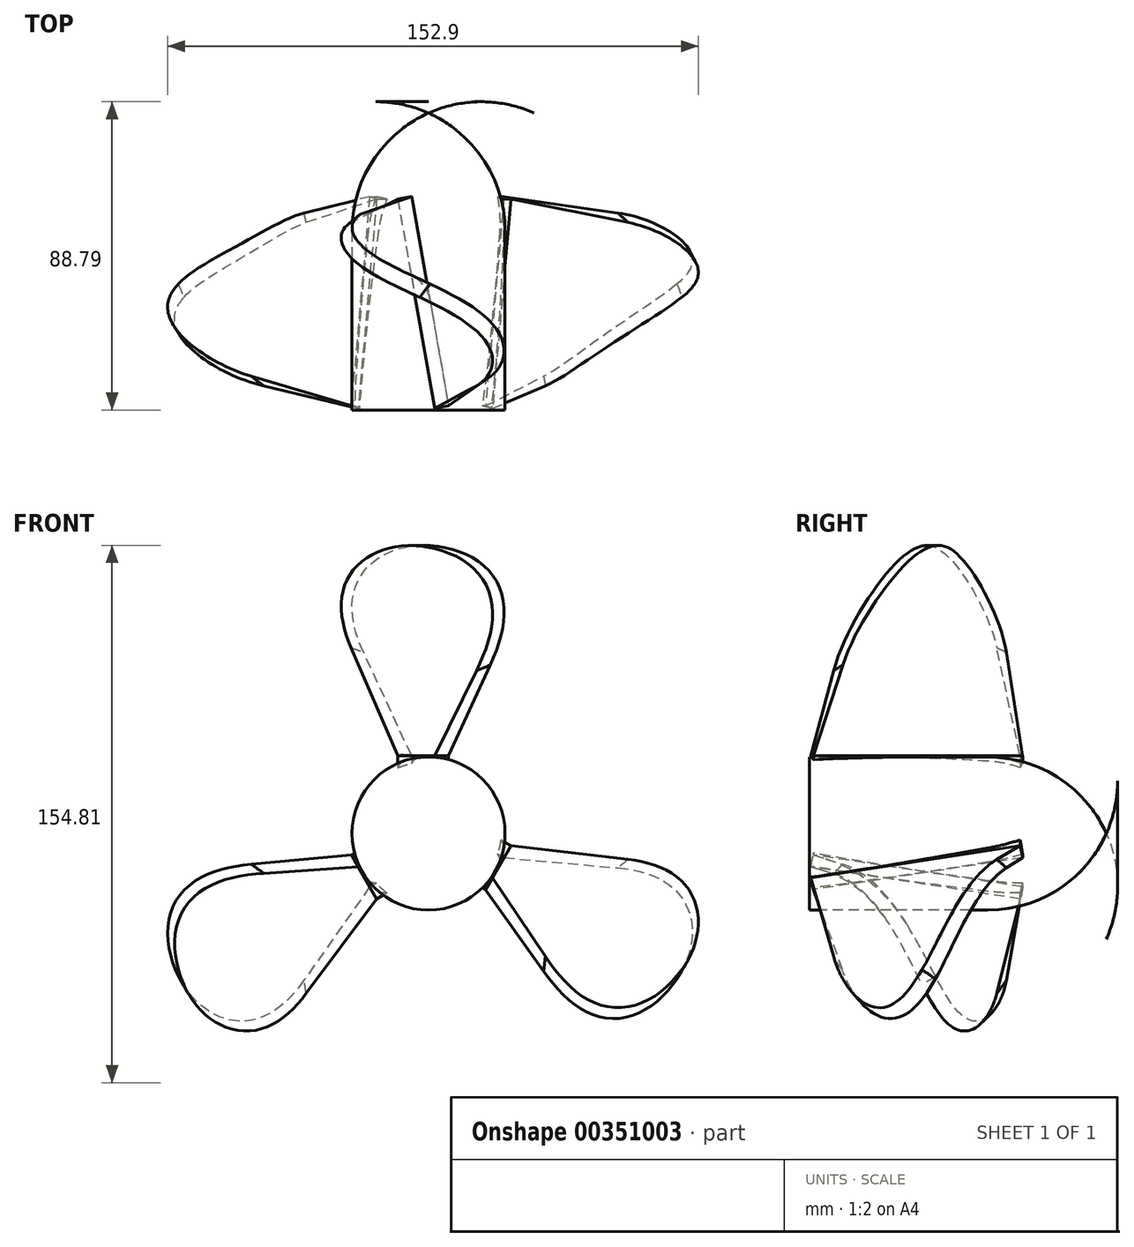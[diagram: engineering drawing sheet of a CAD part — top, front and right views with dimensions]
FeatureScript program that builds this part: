
annotation { "Feature Type Name" : "Feature", "Feature Type Description" : "" }
export const myFeature = defineFeature(function(context is Context, id is Id, definition is map)
    precondition{}
    {
        {
            var Q0;
            Q0=qCreatedBy(makeId("Right.planeOp"),FACE);
            var sketch = newSketch(context, id + "F0", { "sketchPlane" : qUnion([Q0])});
            skLineSegment(sketch, "E0", {"start": v(-50.75, 0) * mm, "end": v(-50.75, 22.06) * mm});
            skLineSegment(sketch, "E1", {"start": v(-50.75, 22.06) * mm, "end": v(0, 22.06) * mm});
            skLineSegment(sketch, "E2", {"start": v(-50.75, 0) * mm, "end": v(34.03, 0) * mm});
            skArc(sketch, "E3", {"start": v(34.03, 0) * mm, "mid": v(20.28, 16.06) * mm, "end": v(0, 22.06) * mm});
            skSolve(sketch);
        }
        {
            var Q0;
            Q0=makeQuery(id+"F0.imprint","IMPRINT",FACE,{"disambiguationData":[TD([[makeQuery(id+"F0.imprint","IMPRINT",EDGE,{"derivedFrom":sQuery(id+"F0.wireOp",EDGE,"E0")}),-1.0]])]});
            var Q1;
            Q1=sQuery(id+"F0.wireOp",EDGE,"E2");
            revolve(context, id + "F1", {"entities" : qUnion([Q0]), "axis" : qUnion([Q1]), "revolveType" : RevolveType.FULL});
        }
        {
            var Q0;
            Q0=qCreatedBy(makeId("Top.planeOp"),FACE);
            var sketch = newSketch(context, id + "F2", { "sketchPlane" : qUnion([Q0])});
            skLineSegment(sketch, "E4.bottom", {"start": v(-8.85, 9.23) * mm, "end": v(-4.85, 9.93) * mm});
            skLineSegment(sketch, "E4.top", {"start": v(1.78, -51.05) * mm, "end": v(5.78, -50.34) * mm});
            skLineSegment(sketch, "E4.left", {"start": v(-8.85, 9.23) * mm, "end": v(1.78, -51.05) * mm});
            skLineSegment(sketch, "E4.right", {"start": v(-4.85, 9.93) * mm, "end": v(5.78, -50.34) * mm});
            skSolve(sketch);
        }
        {
            var Q0;
            Q0=qCreatedBy(makeId("Top.planeOp"),FACE);
            cPlane(context, id + "F3", {"entities" : qUnion([Q0]), "cplaneType" : CPlaneType.OFFSET, "offset" : 83.06 * mm, "width" : 152.4 * mm, "height" : 152.4 * mm});
        }
        {
            var Q0;
            Q0=qCreatedBy(id+"F3.planeOp",FACE);
            var sketch = newSketch(context, id + "F4", { "sketchPlane" : qUnion([Q0])});
            skLineSegment(sketch, "E5.bottom", {"start": v(-35.01, -3.9) * mm, "end": v(-33, 0.4) * mm});
            skLineSegment(sketch, "E5.top", {"start": v(31.59, -34.96) * mm, "end": v(33.6, -30.66) * mm});
            skLineSegment(sketch, "E5.left", {"start": v(-35.01, -3.9) * mm, "end": v(31.59, -34.96) * mm});
            skLineSegment(sketch, "E5.right", {"start": v(-33, 0.4) * mm, "end": v(33.6, -30.66) * mm});
            skSolve(sketch);
        }
        {
            var Q0;
            Q0=makeQuery(id+"F1.opRevolve","SWEPT_FACE",FACE,{"disambiguationData":[OSD([sQuery(id+"F0.wireOp",EDGE,"E0")])]});
            extrude(context, id + "F5", {"entities" : qUnion([Q0]), "operationType" : NewBodyOperationType.ADD, "depth" : 15.24 * mm});
        }
        {
            var Q0;
            Q0 = qSketchRegion(id + "F2", true);
            extrude(context, id + "F6", {"entities" : qUnion([Q0]), "operationType" : NewBodyOperationType.ADD, "depth" : 22.35 * mm});
        }
        {
            var Q1;
            Q1=makeQuery(id+"F6.opExtrude","CAP_FACE",FACE,{"disambiguationData":[OSD([sQuery(id+"F2.wireOp",EDGE,"E4.bottom"),sQuery(id+"F2.wireOp",EDGE,"E4.top"),sQuery(id+"F2.wireOp",EDGE,"E4.left"),sQuery(id+"F2.wireOp",EDGE,"E4.right")])],"isStart":false});
            var Q2;
            Q2=makeQuery(id+"F4.imprint","IMPRINT",FACE,{"disambiguationData":[TD([[makeQuery(id+"F4.imprint","IMPRINT",EDGE,{"derivedFrom":sQuery(id+"F4.wireOp",EDGE,"E5.bottom")}),-1.0]])]});
            loft(context, id + "F7", {"operationType" : NewBodyOperationType.ADD, "sheetProfilesArray" : [{ "sheetProfileEntities" : qUnion([Q1]) }, { "sheetProfileEntities" : qUnion([Q2]) }]});
        }
        {
            var Q0;
            Q0=makeQuery(id+"F7.opLoft","MID_CAP_EDGE",EDGE,{"disambiguationData":[OSD([sQuery(id+"F4.wireOp",EDGE,"E5.top"),sQuery(id+"F4.wireOp",EDGE,"E5.left"),sQuery(id+"F4.wireOp",EDGE,"E5.right")])],"capPos":1.0});
            fillet(context, id + "F8", {"entities" : qUnion([Q0]), "radius" : 34.31 * mm, "tangentPropagation" : true, "allowEdgeOverflow" : false});
        }
        {
            var Q0;
            Q0=makeQuery(id+"F7.opLoft","MID_CAP_EDGE",EDGE,{"disambiguationData":[OSD([sQuery(id+"F4.wireOp",EDGE,"E5.bottom"),sQuery(id+"F4.wireOp",EDGE,"E5.left"),sQuery(id+"F4.wireOp",EDGE,"E5.right")])],"capPos":1.0});
            fillet(context, id + "F9", {"entities" : qUnion([Q0]), "radius" : 26.37 * mm, "tangentPropagation" : true, "allowEdgeOverflow" : false});
        }
        {
            var Q0;
            Q0=makeQuery(id+"F5.opExtrude","CAP_FACE",FACE,{"disambiguationData":[OSD([sQuery(id+"F0.wireOp",EDGE,"E0")])],"isStart":false});
            extrude(context, id + "F10", {"entities" : qUnion([Q0]), "operationType" : NewBodyOperationType.REMOVE, "oppositeDirection" : true, "depth" : 14.48 * mm});
        }
        {
            var Q0;
            Q0=makeQuery(id+"F1.opRevolve","SWEPT_BODY",BODY,{"disambiguationData":[OSD([sQuery(id+"F0.wireOp",EDGE,"E0"),sQuery(id+"F0.wireOp",EDGE,"E1"),sQuery(id+"F0.wireOp",EDGE,"E2"),sQuery(id+"F0.wireOp",EDGE,"E3")])]});
            var Q1;
            Q1=sQuery(id+"F0.wireOp",EDGE,"E2");
            circularPattern(context, id + "F11", {"entities" : qUnion([Q0]), "axis" : qUnion([Q1]), "angle" : 360 * degree, "instanceCount" : 3, "equalSpace" : true});
        }
        {
            var Q0;
            {var subQ0=sQuery(id+"F2.wireOp",EDGE,"E4.bottom");Q0=makeQuery(id+"F7.boolean.opBoolean","MERGE",EDGE,{"derivedFrom":[makeQuery(id+"F6.opExtrude","CAP_EDGE",EDGE,{"disambiguationData":[OSD([subQ0])],"isStart":false}),makeQuery(id+"F7.opLoft","MID_CAP_EDGE",EDGE,{"disambiguationData":[OSD([subQ0,sQuery(id+"F2.wireOp",EDGE,"E4.left"),sQuery(id+"F2.wireOp",EDGE,"E4.right")])],"capPos":0.0})]});}
            fillet(context, id + "F12", {"entities" : qUnion([Q0]), "radius" : 7.15 * mm, "tangentPropagation" : true, "allowEdgeOverflow" : false});
        }
    });
